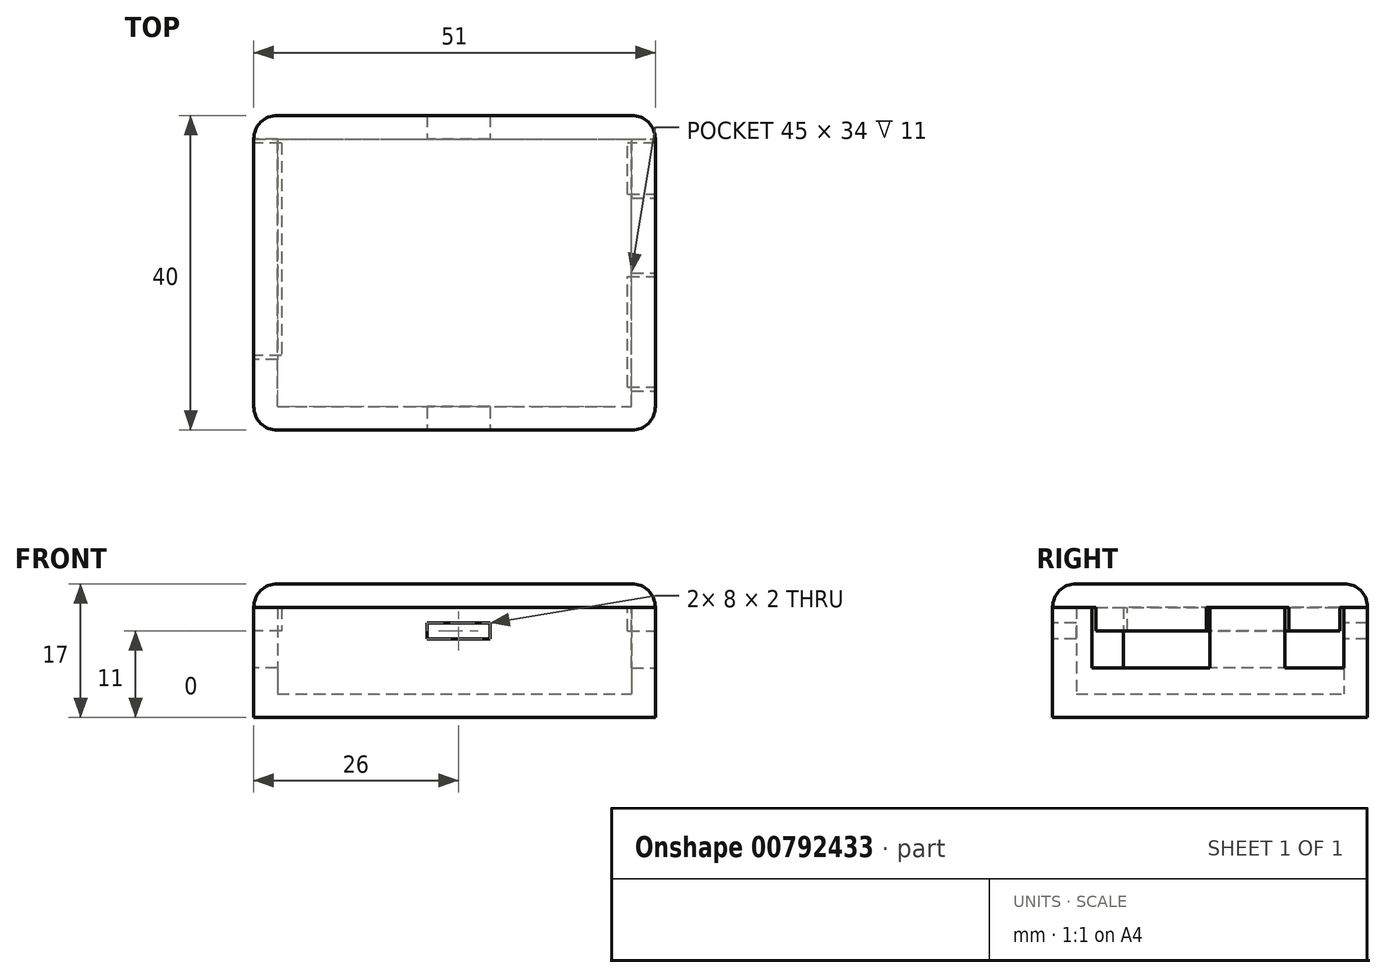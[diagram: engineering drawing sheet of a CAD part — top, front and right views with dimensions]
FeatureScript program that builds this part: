
annotation { "Feature Type Name" : "Feature", "Feature Type Description" : "" }
export const myFeature = defineFeature(function(context is Context, id is Id, definition is map)
    precondition{}
    {
        {
            var Q0;
            Q0=qCreatedBy(makeId("Top.planeOp"),FACE);
            var sketch = newSketch(context, id + "F0", { "sketchPlane" : qUnion([Q0])});
            skLineSegment(sketch, "E0.bottom", {"start": v(0, 0) * mm, "end": v(51, 0) * mm});
            skLineSegment(sketch, "E0.top", {"start": v(0, 40) * mm, "end": v(51, 40) * mm});
            skLineSegment(sketch, "E0.left", {"start": v(0, 0) * mm, "end": v(0, 40) * mm});
            skLineSegment(sketch, "E0.right", {"start": v(51, 0) * mm, "end": v(51, 40) * mm});
            skSolve(sketch);
        }
        {
            var Q0;
            Q0=qSketchRegion(id+"F0",true);
            extrude(context, id + "F1", {"entities" : qUnion([Q0]), "depth" : 14 * mm, "offsetDistance" : 25 * mm});
        }
        {
            var Q0;
            Q0=makeQuery(id+"F1.opExtrude","CAP_FACE",FACE,{"disambiguationData":[OSD([sQuery(id+"F0.wireOp",EDGE,"E0.bottom"),sQuery(id+"F0.wireOp",EDGE,"E0.top"),sQuery(id+"F0.wireOp",EDGE,"E0.left"),sQuery(id+"F0.wireOp",EDGE,"E0.right")])],"isStart":false});
            shell(context, id + "F2", {"entities" : qUnion([Q0]), "thickness" : 3 * mm});
        }
        {
            var Q0;
            Q0=makeQuery(id+"F1.opExtrude","SWEPT_FACE",FACE,{"disambiguationData":[OSD([sQuery(id+"F0.wireOp",EDGE,"E0.right")])]});
            var sketch = newSketch(context, id + "F3", { "sketchPlane" : qUnion([Q0])});
            skLineSegment(sketch, "E1.bottom", {"start": v(29.5, 14) * mm, "end": v(37, 14) * mm});
            skLineSegment(sketch, "E1.top", {"start": v(29.5, 6.3) * mm, "end": v(37, 6.3) * mm});
            skLineSegment(sketch, "E1.left", {"start": v(29.5, 14) * mm, "end": v(29.5, 6.3) * mm});
            skLineSegment(sketch, "E1.right", {"start": v(37, 14) * mm, "end": v(37, 6.3) * mm});
            skLineSegment(sketch, "E2.bottom", {"start": v(20, 14) * mm, "end": v(5, 14) * mm});
            skLineSegment(sketch, "E2.top", {"start": v(20, 6.3) * mm, "end": v(5, 6.3) * mm});
            skLineSegment(sketch, "E2.left", {"start": v(20, 14) * mm, "end": v(20, 6.3) * mm});
            skLineSegment(sketch, "E2.right", {"start": v(5, 14) * mm, "end": v(5, 6.3) * mm});
            skSolve(sketch);
        }
        {
            var Q0;
            Q0=qSketchRegion(id+"F3",true);
            extrude(context, id + "F4", {"entities" : qUnion([Q0]), "operationType" : NewBodyOperationType.REMOVE, "oppositeDirection" : true, "depth" : 25 * mm, "offsetDistance" : 25 * mm});
        }
        {
            var Q0;
            Q0=makeQuery(id+"F1.opExtrude","SWEPT_FACE",FACE,{"disambiguationData":[OSD([sQuery(id+"F0.wireOp",EDGE,"E0.left")])]});
            var sketch = newSketch(context, id + "F5", { "sketchPlane" : qUnion([Q0])});
            skLineSegment(sketch, "E3.bottom", {"start": v(-37, 14) * mm, "end": v(-9, 14) * mm});
            skLineSegment(sketch, "E3.top", {"start": v(-37, 6.3) * mm, "end": v(-9, 6.3) * mm});
            skLineSegment(sketch, "E3.left", {"start": v(-37, 14) * mm, "end": v(-37, 6.3) * mm});
            skLineSegment(sketch, "E3.right", {"start": v(-9, 14) * mm, "end": v(-9, 6.3) * mm});
            skSolve(sketch);
        }
        {
            var Q0;
            Q0=qSketchRegion(id+"F5",true);
            extrude(context, id + "F6", {"entities" : qUnion([Q0]), "operationType" : NewBodyOperationType.REMOVE, "oppositeDirection" : true, "depth" : 25 * mm, "offsetDistance" : 25 * mm});
        }
        {
            var Q0;
            Q0=makeQuery(id+"F1.opExtrude","SWEPT_FACE",FACE,{"disambiguationData":[OSD([sQuery(id+"F0.wireOp",EDGE,"E0.bottom")])]});
            var sketch = newSketch(context, id + "F7", { "sketchPlane" : qUnion([Q0])});
            skLineSegment(sketch, "E4.bottom", {"start": v(22, 12) * mm, "end": v(30, 12) * mm});
            skLineSegment(sketch, "E4.top", {"start": v(22, 10) * mm, "end": v(30, 10) * mm});
            skLineSegment(sketch, "E4.left", {"start": v(22, 12) * mm, "end": v(22, 10) * mm});
            skLineSegment(sketch, "E4.right", {"start": v(30, 12) * mm, "end": v(30, 10) * mm});
            skSolve(sketch);
        }
        {
            var Q0;
            Q0=qSketchRegion(id+"F7",true);
            extrude(context, id + "F8", {"entities" : qUnion([Q0]), "operationType" : NewBodyOperationType.REMOVE, "endBound" : BoundingType.THROUGH_ALL, "oppositeDirection" : true, "depth" : 25 * mm, "offsetDistance" : 25 * mm});
        }
        {
            var Q0;
            Q0=makeQuery(id+"F1.opExtrude","SWEPT_EDGE",EDGE,{"disambiguationData":[OSD([sQuery(id+"F0.wireOp",EDGE,"E0.bottom"),sQuery(id+"F0.wireOp",EDGE,"E0.left")])]});
            var Q1;
            Q1=makeQuery(id+"F1.opExtrude","SWEPT_EDGE",EDGE,{"disambiguationData":[OSD([sQuery(id+"F0.wireOp",EDGE,"E0.bottom"),sQuery(id+"F0.wireOp",EDGE,"E0.right")])]});
            var Q2;
            Q2=makeQuery(id+"F1.opExtrude","SWEPT_EDGE",EDGE,{"disambiguationData":[OSD([sQuery(id+"F0.wireOp",EDGE,"E0.top"),sQuery(id+"F0.wireOp",EDGE,"E0.right")])]});
            var Q3;
            Q3=makeQuery(id+"F1.opExtrude","SWEPT_EDGE",EDGE,{"disambiguationData":[OSD([sQuery(id+"F0.wireOp",EDGE,"E0.top"),sQuery(id+"F0.wireOp",EDGE,"E0.left")])]});
            fillet(context, id + "F9", {"entities" : qUnion([Q0, Q1, Q2, Q3]), "radius" : 3 * mm, "tangentPropagation" : true, "allowEdgeOverflow" : false});
        }
        {
            var Q0;
            {var subQ0=sQuery(id+"F0.wireOp",EDGE,"E0.right");var subQ2=sQuery(id+"F0.wireOp",EDGE,"E0.left");var subQ4=sQuery(id+"F0.wireOp",EDGE,"E0.top");var subQ6=makeQuery(id+"F1.opExtrude","SWEPT_FACE",FACE,{"disambiguationData":[OSD([subQ4])]});var subQ8=sQuery(id+"F0.wireOp",EDGE,"E0.bottom");Q0=makeQuery(id+"F6.boolean.opBoolean","SPLIT",FACE,{"disambiguationData":[TD([subQ6])],"derivedFrom":makeQuery(id+"F4.boolean.opBoolean","SPLIT",FACE,{"disambiguationData":[TD([makeQuery(id+"F1.opExtrude","SWEPT_FACE",FACE,{"disambiguationData":[OSD([subQ8])]})])],"derivedFrom":makeQuery(id+"F1.opExtrude","CAP_FACE",FACE,{"disambiguationData":[OSD([subQ8,subQ4,subQ2,subQ0])],"isStart":false})})});}
            var sketch = newSketch(context, id + "F10", { "sketchPlane" : qUnion([Q0])});
            skLineSegment(sketch, "E5.bottom", {"start": v(0, 0) * mm, "end": v(51, 0) * mm});
            skLineSegment(sketch, "E5.top", {"start": v(0, 40) * mm, "end": v(51, 40) * mm});
            skLineSegment(sketch, "E5.left", {"start": v(0, 0) * mm, "end": v(0, 40) * mm});
            skLineSegment(sketch, "E5.right", {"start": v(51, 0) * mm, "end": v(51, 40) * mm});
            skSolve(sketch);
        }
        {
            var Q0;
            Q0=qSketchRegion(id+"F10",true);
            extrude(context, id + "F11", {"entities" : qUnion([Q0]), "depth" : 3 * mm, "offsetDistance" : 25 * mm});
        }
        {
            var Q0;
            Q0=makeQuery(id+"F11.opExtrude","CAP_FACE",FACE,{"disambiguationData":[OSD([sQuery(id+"F10.wireOp",EDGE,"E5.bottom"),sQuery(id+"F10.wireOp",EDGE,"E5.top"),sQuery(id+"F10.wireOp",EDGE,"E5.left"),sQuery(id+"F10.wireOp",EDGE,"E5.right")])],"isStart":true});
            var sketch = newSketch(context, id + "F12", { "sketchPlane" : qUnion([Q0])});
            skLineSegment(sketch, "E6.bottom", {"start": v(3.5, -36.5) * mm, "end": v(47.5, -36.5) * mm});
            skLineSegment(sketch, "E6.top", {"start": v(3.5, -3.5) * mm, "end": v(47.5, -3.5) * mm});
            skLineSegment(sketch, "E6.left", {"start": v(3.5, -9.5) * mm, "end": v(3.5, -3.5) * mm});
            skLineSegment(sketch, "E6.right", {"start": v(47.5, -30) * mm, "end": v(47.5, -19.5) * mm});
            skLineSegment(sketch, "E7.bottom", {"start": v(3.5, -36.5) * mm, "end": v(0, -36.5) * mm});
            skLineSegment(sketch, "E7.top", {"start": v(3.5, -9.5) * mm, "end": v(0, -9.5) * mm});
            skLineSegment(sketch, "E7.right", {"start": v(0, -36.5) * mm, "end": v(0, -9.5) * mm});
            skLineSegment(sketch, "E8.bottom", {"start": v(47.5, -19.5) * mm, "end": v(51, -19.5) * mm});
            skLineSegment(sketch, "E8.top", {"start": v(47.5, -5.5) * mm, "end": v(51, -5.5) * mm});
            skLineSegment(sketch, "E8.right", {"start": v(51, -19.5) * mm, "end": v(51, -5.5) * mm});
            skLineSegment(sketch, "E9.bottom", {"start": v(47.5, -30) * mm, "end": v(51, -30) * mm});
            skLineSegment(sketch, "E9.top", {"start": v(47.5, -36.5) * mm, "end": v(51, -36.5) * mm});
            skLineSegment(sketch, "E9.right", {"start": v(51, -30) * mm, "end": v(51, -36.5) * mm});
            skLineSegment(sketch, "E10.trimOffspring", {"start": v(47.5, -5.5) * mm, "end": v(47.5, -3.5) * mm});
            skSolve(sketch);
        }
        {
            var Q0;
            Q0=qSketchRegion(id+"F12",true);
            extrude(context, id + "F13", {"entities" : qUnion([Q0]), "operationType" : NewBodyOperationType.ADD, "depth" : 3 * mm, "offsetDistance" : 25 * mm});
        }
        {
            var Q0;
            Q0=makeQuery(id+"F13.opExtrude","CAP_FACE",FACE,{"disambiguationData":[OSD([sQuery(id+"F12.wireOp",EDGE,"E6.bottom"),sQuery(id+"F12.wireOp",EDGE,"E6.top"),sQuery(id+"F12.wireOp",EDGE,"E6.left"),sQuery(id+"F12.wireOp",EDGE,"E6.right"),sQuery(id+"F12.wireOp",EDGE,"E7.bottom"),sQuery(id+"F12.wireOp",EDGE,"E7.top"),sQuery(id+"F12.wireOp",EDGE,"E7.right"),sQuery(id+"F12.wireOp",EDGE,"E8.bottom"),sQuery(id+"F12.wireOp",EDGE,"E8.top"),sQuery(id+"F12.wireOp",EDGE,"E8.right"),sQuery(id+"F12.wireOp",EDGE,"E9.bottom"),sQuery(id+"F12.wireOp",EDGE,"E9.top"),sQuery(id+"F12.wireOp",EDGE,"E9.right"),sQuery(id+"F12.wireOp",EDGE,"E10.trimOffspring")])],"isStart":false});
            var sketch = newSketch(context, id + "F14", { "sketchPlane" : qUnion([Q0])});
            skLineSegment(sketch, "E11.bottom", {"start": v(3.5, -3.5) * mm, "end": v(47.5, -3.5) * mm});
            skLineSegment(sketch, "E11.top", {"start": v(3.5, -36.5) * mm, "end": v(47.5, -36.5) * mm});
            skLineSegment(sketch, "E11.left", {"start": v(3.5, -3.5) * mm, "end": v(3.5, -36.5) * mm});
            skLineSegment(sketch, "E11.right", {"start": v(47.5, -3.5) * mm, "end": v(47.5, -36.5) * mm});
            skSolve(sketch);
        }
        {
            var Q0;
            Q0=qSketchRegion(id+"F14",true);
            extrude(context, id + "F15", {"entities" : qUnion([Q0]), "operationType" : NewBodyOperationType.REMOVE, "oppositeDirection" : true, "depth" : 3 * mm, "offsetDistance" : 25 * mm});
        }
        {
            var Q0;
            Q0=makeQuery(id+"F11.opExtrude","SWEPT_EDGE",EDGE,{"disambiguationData":[OSD([sQuery(id+"F10.wireOp",EDGE,"E5.top"),sQuery(id+"F10.wireOp",EDGE,"E5.left")])]});
            var Q1;
            Q1=makeQuery(id+"F11.opExtrude","SWEPT_EDGE",EDGE,{"disambiguationData":[OSD([sQuery(id+"F10.wireOp",EDGE,"E5.top"),sQuery(id+"F10.wireOp",EDGE,"E5.right")])]});
            var Q2;
            Q2=makeQuery(id+"F11.opExtrude","CAP_EDGE",EDGE,{"disambiguationData":[OSD([sQuery(id+"F10.wireOp",EDGE,"E5.top")])],"isStart":false});
            var Q3;
            Q3=makeQuery(id+"F11.opExtrude","CAP_EDGE",EDGE,{"disambiguationData":[OSD([sQuery(id+"F10.wireOp",EDGE,"E5.right")])],"isStart":false});
            var Q4;
            Q4=makeQuery(id+"F11.opExtrude","SWEPT_EDGE",EDGE,{"disambiguationData":[OSD([sQuery(id+"F10.wireOp",EDGE,"E5.bottom"),sQuery(id+"F10.wireOp",EDGE,"E5.left")])]});
            var Q5;
            Q5=makeQuery(id+"F11.opExtrude","CAP_EDGE",EDGE,{"disambiguationData":[OSD([sQuery(id+"F10.wireOp",EDGE,"E5.left")])],"isStart":false});
            var Q6;
            Q6=makeQuery(id+"F11.opExtrude","CAP_EDGE",EDGE,{"disambiguationData":[OSD([sQuery(id+"F10.wireOp",EDGE,"E5.bottom")])],"isStart":false});
            var Q7;
            Q7=makeQuery(id+"F11.opExtrude","SWEPT_EDGE",EDGE,{"disambiguationData":[OSD([sQuery(id+"F10.wireOp",EDGE,"E5.bottom"),sQuery(id+"F10.wireOp",EDGE,"E5.right")])]});
            fillet(context, id + "F16", {"entities" : qUnion([Q0, Q1, Q2, Q3, Q4, Q5, Q6, Q7]), "radius" : 3 * mm, "tangentPropagation" : true, "allowEdgeOverflow" : false});
        }
    });
